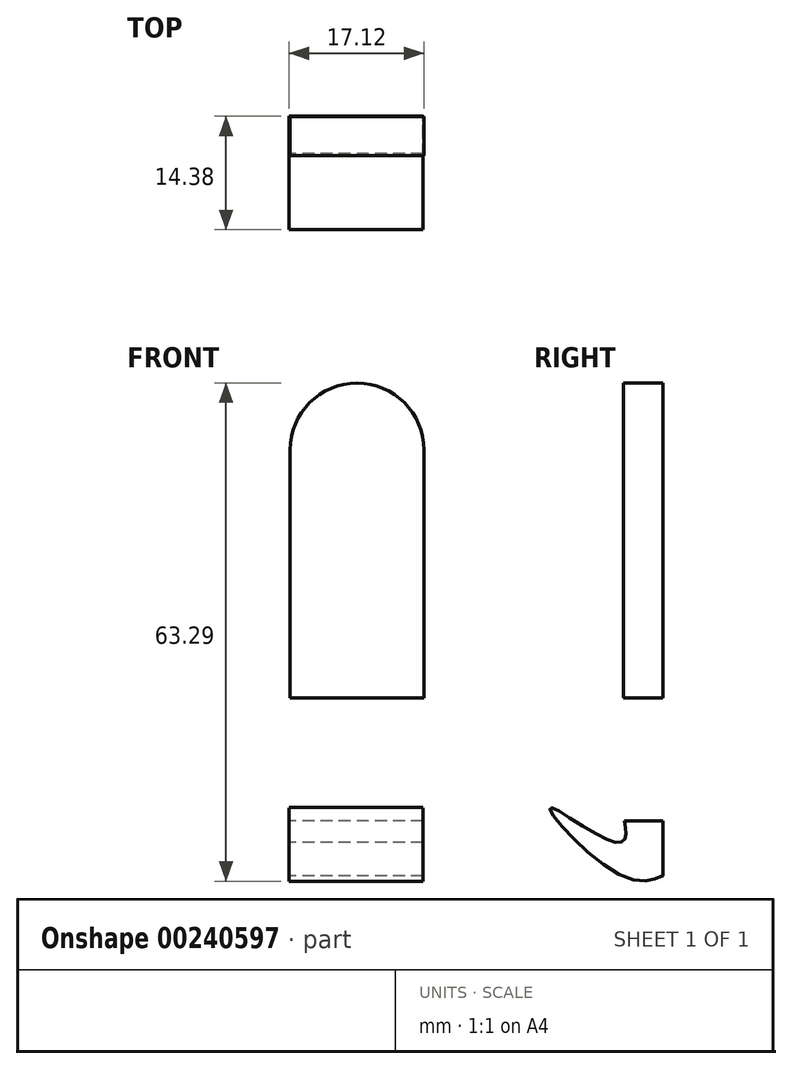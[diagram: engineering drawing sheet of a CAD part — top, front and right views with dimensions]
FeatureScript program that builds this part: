
annotation { "Feature Type Name" : "Feature", "Feature Type Description" : "" }
export const myFeature = defineFeature(function(context is Context, id is Id, definition is map)
    precondition{}
    {
        {
            var Q0;
            Q0=qCreatedBy(makeId("Front.planeOp"),FACE);
            var sketch = newSketch(context, id + "F0", { "sketchPlane" : qUnion([Q0])});
            skLineSegment(sketch, "E0", {"start": v(-8.38, 24.9) * mm, "end": v(-8.38, -6.6) * mm});
            skLineSegment(sketch, "E1", {"start": v(8.62, -6.6) * mm, "end": v(8.62, 24.9) * mm});
            skLineSegment(sketch, "E2", {"start": v(0.12, 24.9) * mm, "end": v(0.12, 24.9) * mm});
            skArc(sketch, "E3", {"start": v(8.62, 24.9) * mm, "mid": v(0.12, 33.4) * mm, "end": v(-8.38, 24.9) * mm});
            skLineSegment(sketch, "E4", {"start": v(-8.38, -6.6) * mm, "end": v(8.62, -6.6) * mm});
            skPoint(sketch, "E5.end.orphan", {"position": v(0, -34.5) * mm});
            skSolve(sketch);
        }
        {
            var Q0;
            Q0=makeQuery(id+"F0.imprint","IMPRINT",FACE,{"disambiguationData":[TD([[makeQuery(id+"F0.imprint","IMPRINT",EDGE,{"derivedFrom":sQuery(id+"F0.wireOp",EDGE,"E0")}),1.0]])]});
            var Q1;
            Q1=makeQuery(id+"F0.imprint","IMPRINT",FACE,{"disambiguationData":[TD([[makeQuery(id+"F0.imprint","IMPRINT",EDGE,{"derivedFrom":sQuery(id+"F0.wireOp",EDGE,"E4")}),-1.0]])]});
            extrude(context, id + "F1", {"entities" : qUnion([Q0, Q1]), "depth" : 5 * mm});
        }
        {
            var Q0;
            Q0=qCreatedBy(makeId("Right.planeOp"),FACE);
            var sketch = newSketch(context, id + "F2", { "sketchPlane" : qUnion([Q0])});
            skFitSpline(sketch, "E6", {"points": [v(-4.93, -22.2) * mm, v(-4.84, -24.54) * mm, v(-7.06, -24.63) * mm, v(-14.36, -20.59) * mm, v(-3.88, -29.71) * mm, v(0, -29.2) * mm, v(0, -29.32) * mm], "startDerivative": vector(4.23, -21.43) * mm, "endDerivative": vector(-1.42, -5.42) * mm});
            skLineSegment(sketch, "E7", {"start": v(0.01, -29.27) * mm, "end": v(0.01, -22.23) * mm});
            skLineSegment(sketch, "E8", {"start": v(-4.93, -22.2) * mm, "end": v(0.01, -22.23) * mm});
            skSolve(sketch);
        }
        {
            var Q0;
            {var subQ0=sQuery(id+"F2.wireOp",EDGE,"E8");Q0=makeQuery(id+"F2.imprint","IMPRINT",FACE,{"disambiguationData":[TD([[makeQuery(id+"F2.imprint","IMPRINT",EDGE,{"derivedFrom":subQ0}),-1.0]])]});}
            extrude(context, id + "F3", {"entities" : qUnion([Q0]), "endBound" : BoundingType.SYMMETRIC, "depth" : 17 * mm});
        }
    });
